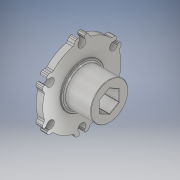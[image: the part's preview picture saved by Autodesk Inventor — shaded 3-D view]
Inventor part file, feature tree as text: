
AUTODESK INVENTOR PART (.ipt)
format: ipt  version: 2017.1 (Build 211199000, 199)  size: 281,600 bytes
history: native  units: in
note: dims shown in document units (in); Inventor stores cm internally (conversion verified against a paired STEP export)
features: fillet x1
ambient origin geometry x8: Origin, YZ Plane, XZ Plane, XY Plane, X Axis, Y Axis, Z Axis, Center Point
bodies: Solid1 (feature_tree)
feature tree (1):
  fillet  "Fillet7"  [1 undecoded]
note: 1 required parameter value undecoded (feature->parameter linkage not recoverable at this tier; creation-order binding heuristic only, values carry confidence <= 0.55)
